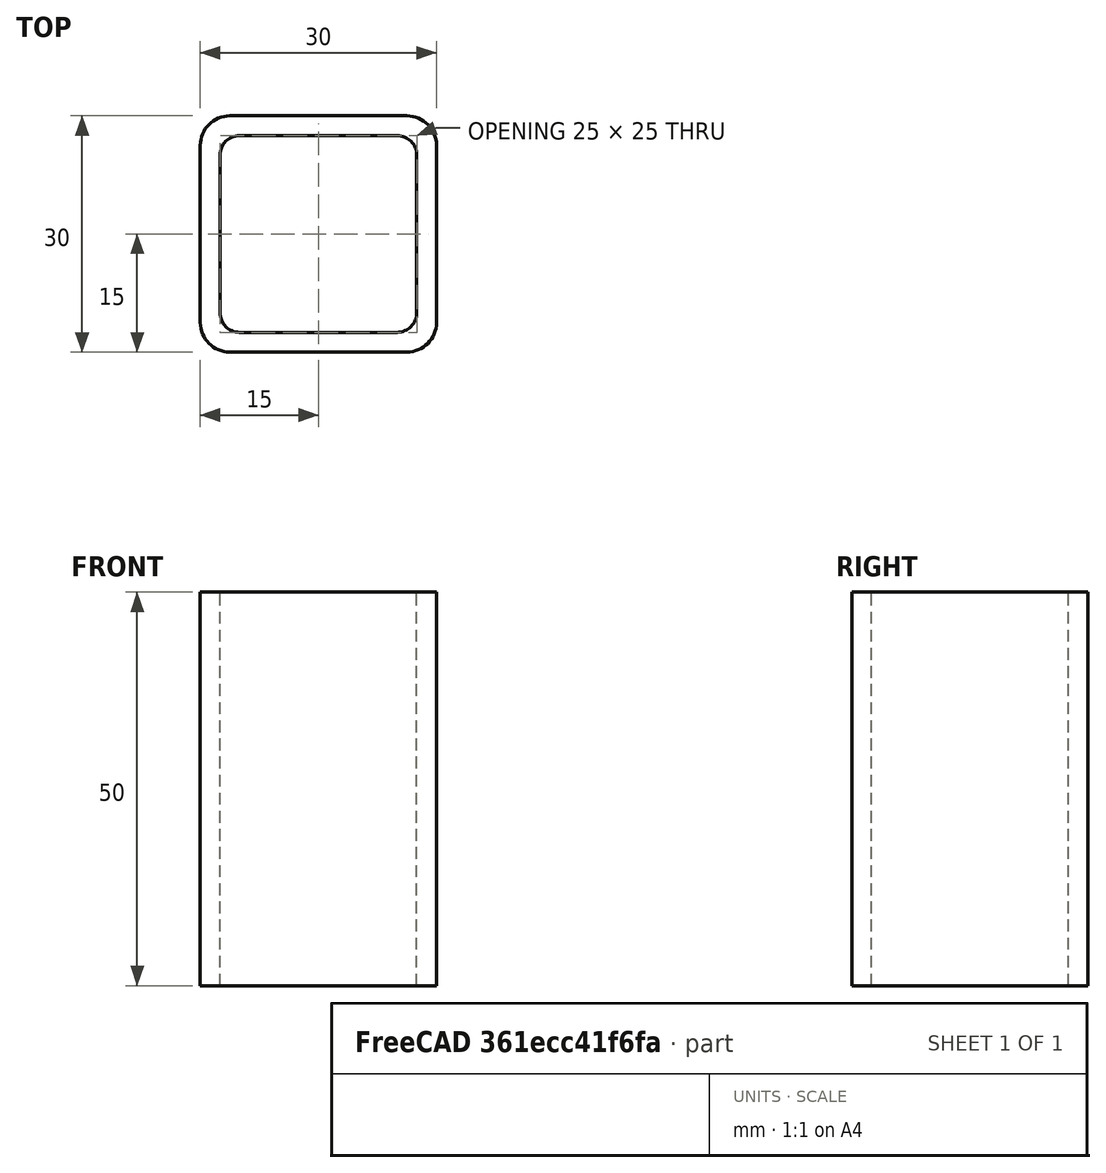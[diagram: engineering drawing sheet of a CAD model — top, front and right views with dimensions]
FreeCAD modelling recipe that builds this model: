
FCSTD DOCUMENT  (FreeCAD 0.15R4671 (Git))
Label: Square hollow section 30x30x2.5 EN10219 S235JRH
License: All rights reserved
LicenseURL: http://en.wikipedia.org/wiki/All_rights_reserved
objects: Sketcher::SketchObject×1, Part::Extrusion×1
note: 2 computed .brp shape members not serialized (recipe doc carries the construction recipe); baked Part::Feature solids carry a one-line shape summary decoded from their .brp

FEATURE [Sketcher::SketchObject] Sketch
  sketch-geometry (16):
    g0: LineSegment StartX=-10 StartY=12.5 StartZ=0 EndX=10 EndY=12.5 EndZ=0
    g1: LineSegment StartX=12.5 StartY=10 StartZ=0 EndX=12.5 EndY=-10 EndZ=0
    g2: LineSegment StartX=10 StartY=-12.5 StartZ=0 EndX=-10 EndY=-12.5 EndZ=0
    g3: LineSegment StartX=-12.5 StartY=-10 StartZ=0 EndX=-12.5 EndY=10 EndZ=0
    g4: LineSegment StartX=-11.25 StartY=15 StartZ=0 EndX=11.25 EndY=15 EndZ=0
    g5: LineSegment StartX=15 StartY=11.25 StartZ=0 EndX=15 EndY=-11.25 EndZ=0
    g6: LineSegment StartX=11.25 StartY=-15 StartZ=0 EndX=-11.25 EndY=-15 EndZ=0
    g7: LineSegment StartX=-15 StartY=-11.25 StartZ=0 EndX=-15 EndY=11.25 EndZ=0
    g8: ArcOfCircle CenterX=-10 CenterY=10 CenterZ=0 NormalX=0 NormalY=0 NormalZ=1 Radius=2.5 StartAngle=1.5708 EndAngle=3.14159
    g9: ArcOfCircle CenterX=10 CenterY=10 CenterZ=0 NormalX=0 NormalY=0 NormalZ=1 Radius=2.5 StartAngle=0 EndAngle=1.5708
    g10: ArcOfCircle CenterX=10 CenterY=-10 CenterZ=0 NormalX=0 NormalY=0 NormalZ=1 Radius=2.5 StartAngle=4.71239 EndAngle=6.28319
    g11: ArcOfCircle CenterX=-10 CenterY=-10 CenterZ=0 NormalX=0 NormalY=0 NormalZ=1 Radius=2.5 StartAngle=3.14159 EndAngle=4.71239
    g12: ArcOfCircle CenterX=11.25 CenterY=11.25 CenterZ=0 NormalX=0 NormalY=0 NormalZ=1 Radius=3.75 StartAngle=0 EndAngle=1.5708
    g13: ArcOfCircle CenterX=11.25 CenterY=-11.25 CenterZ=0 NormalX=0 NormalY=0 NormalZ=1 Radius=3.75 StartAngle=4.71239 EndAngle=6.28319
    g14: ArcOfCircle CenterX=-11.25 CenterY=-11.25 CenterZ=0 NormalX=0 NormalY=0 NormalZ=1 Radius=3.75 StartAngle=3.14159 EndAngle=4.71239
    g15: ArcOfCircle CenterX=-11.25 CenterY=11.25 CenterZ=0 NormalX=0 NormalY=0 NormalZ=1 Radius=3.75 StartAngle=1.5708 EndAngle=3.14159
  constraints (36):
    c: Horizontal(g2)
    c: Vertical(g3)
    c: Horizontal(g6)
    c: Vertical(g7)
    c: Tangent(g3,g8) = 1.5708
    c: Tangent(g0,g8) = 1.5708
    c: Tangent(g0,g9) = 1.5708
    c: Tangent(g1,g9) = 1.5708
    c: Tangent(g1,g10) = 1.5708
    c: Tangent(g2,g10) = 1.5708
    c: Tangent(g2,g11) = 1.5708
    c: Tangent(g3,g11) = 1.5708
    c: Tangent(g4,g12) = 1.5708
    c: Tangent(g5,g12) = 1.5708
    c: Tangent(g5,g13) = 1.5708
    c: Tangent(g6,g13) = 1.5708
    c: Tangent(g6,g14) = 1.5708
    c: Tangent(g7,g14) = 1.5708
    c: Tangent(g7,g15) = 1.5708
    c: Tangent(g4,g15) = 1.5708
    c: Equal(g9,g8)
    c: Equal(g9,g11)
    c: Equal(g9,g10)
    c: Equal(g12,g15)
    c: Equal(g12,g14)
    c: Equal(g12,g13)
    c: Symmetric(g4,g6,g-1)
    c: Symmetric(g7,g5,g-2)
    c: DistanceY(g4,g6) = -30
    c: DistanceX(g7,g5) = 30
    c: Symmetric(g3,g1,g-2)
    c: Symmetric(g0,g2,g-1)
    c: DistanceY(g0,g4) = 2.5
    c: DistanceX(g5,g1) = -2.5
    c: Radius(g9) = 2.5
    c: Radius(g12) = 3.75
FEATURE [Part::Extrusion] Extrude  label="Square hollow section 30x30x2.5 EN10219 S235JRH"
  Base = -> Sketch
  Dir = (0,0,50)
  Solid = true
